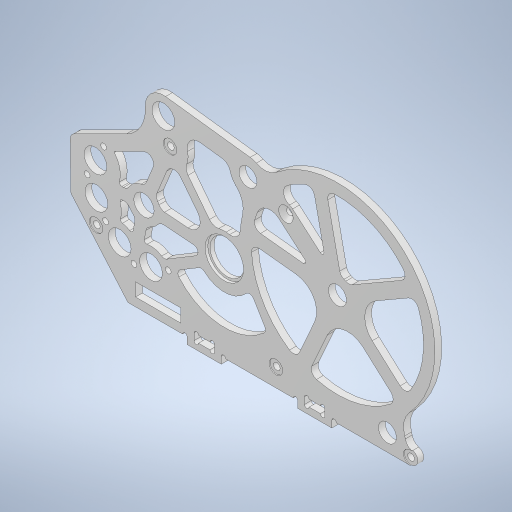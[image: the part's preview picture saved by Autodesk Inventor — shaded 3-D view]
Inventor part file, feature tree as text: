
AUTODESK INVENTOR PART (.ipt)
format: ipt  version: 2023.1 (Build 271208000, 208)  size: 852,480 bytes
history: native  units: mm
features: extrude x4, sketch x2, chamfer x1
ambient origin geometry x8: Origin, YZ Plane, XZ Plane, XY Plane, X Axis, Y Axis, Z Axis, Center Point
bodies: Body1 (feature_tree)
feature tree (7):
  sketch  "スケッチ5"
  extrude  "押し出し3"  Depth=3.0mm TaperAngle=0.0deg
  chamfer  "面取り1"  Distance=3.0mm
  extrude  "押し出し5"  Depth=3.0mm
  extrude  "押し出し6"  Depth=6.0mm
  extrude  "押し出し7"  Depth=1.0mm
  sketch  "スケッチ6"
